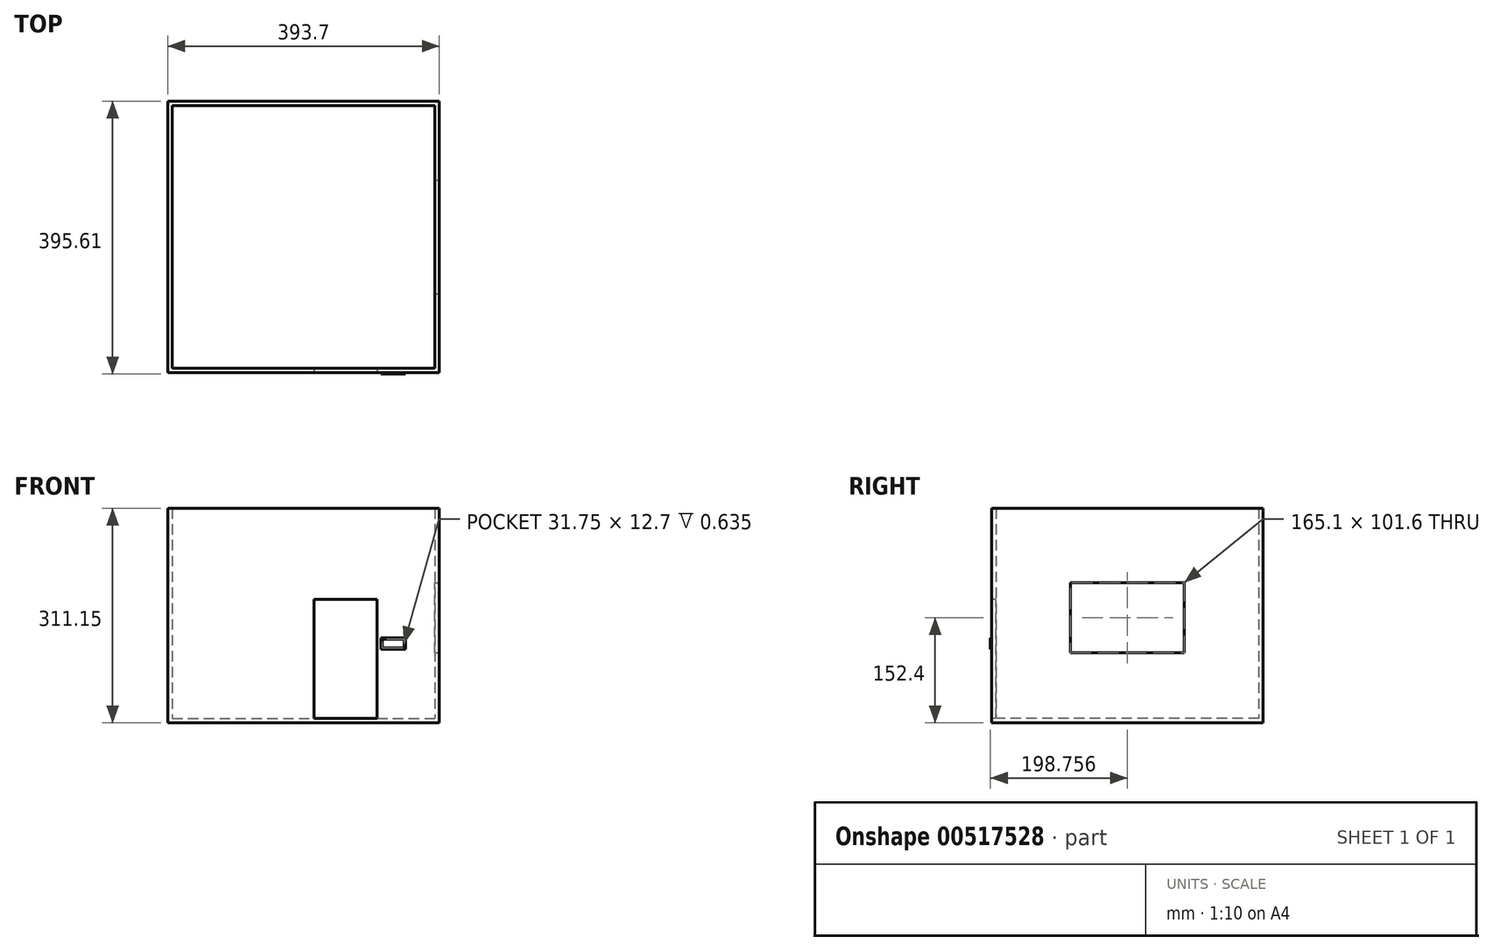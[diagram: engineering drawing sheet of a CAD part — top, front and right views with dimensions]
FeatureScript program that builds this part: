
annotation { "Feature Type Name" : "Feature", "Feature Type Description" : "" }
export const myFeature = defineFeature(function(context is Context, id is Id, definition is map)
    precondition{}
    {
        {
            var Q0;
            Q0=qCreatedBy(makeId("Top.planeOp"),FACE);
            var sketch = newSketch(context, id + "F0", { "sketchPlane" : qUnion([Q0])});
            skLineSegment(sketch, "E0.bottom", {"start": v(-199.94, 305.49) * mm, "end": v(181.06, 305.49) * mm});
            skLineSegment(sketch, "E0.top", {"start": v(-199.94, -75.51) * mm, "end": v(181.06, -75.51) * mm});
            skLineSegment(sketch, "E0.left", {"start": v(-199.94, 305.49) * mm, "end": v(-199.94, -75.51) * mm});
            skLineSegment(sketch, "E0.right", {"start": v(181.06, 305.49) * mm, "end": v(181.06, -75.51) * mm});
            skSolve(sketch);
        }
        {
            var Q0;
            Q0=makeQuery(id+"F0.imprint","IMPRINT",FACE,{"disambiguationData":[TD([[makeQuery(id+"F0.imprint","IMPRINT",EDGE,{"derivedFrom":sQuery(id+"F0.wireOp",EDGE,"E0.bottom")}),-1.0]])]});
            extrude(context, id + "F1", {"entities" : qUnion([Q0]), "depth" : 6.35 * mm, "offsetDistance" : 25.4 * mm});
        }
        {
            var Q0;
            Q0=makeQuery(id+"F1.opExtrude","CAP_FACE",FACE,{"disambiguationData":[OSD([sQuery(id+"F0.wireOp",EDGE,"E0.bottom"),sQuery(id+"F0.wireOp",EDGE,"E0.top"),sQuery(id+"F0.wireOp",EDGE,"E0.left"),sQuery(id+"F0.wireOp",EDGE,"E0.right")])],"isStart":false});
            var sketch = newSketch(context, id + "F2", { "sketchPlane" : qUnion([Q0])});
            skLineSegment(sketch, "E1.0", {"start": v(-206.29, 311.84) * mm, "end": v(187.41, 311.84) * mm});
            skLineSegment(sketch, "E1.1", {"start": v(-206.29, 311.84) * mm, "end": v(-206.29, -81.86) * mm});
            skLineSegment(sketch, "E1.2", {"start": v(-206.29, -81.86) * mm, "end": v(187.41, -81.86) * mm});
            skLineSegment(sketch, "E1.3", {"start": v(187.41, 311.84) * mm, "end": v(187.41, -81.86) * mm});
            skSolve(sketch);
        }
        {
            var Q0;
            Q0=makeQuery(id+"F2.imprint","IMPRINT",FACE,{"disambiguationData":[TD([[makeQuery(id+"F2.imprint","IMPRINT",EDGE,{"derivedFrom":sQuery(id+"F2.wireOp",EDGE,"E1.0")}),-1.0]])]});
            extrude(context, id + "F3", {"entities" : qUnion([Q0]), "operationType" : NewBodyOperationType.ADD, "depth" : 304.8 * mm, "offsetDistance" : 25.4 * mm, "hasSecondDirection" : true, "secondDirectionOppositeDirection" : true, "secondDirectionDepth" : 6.35 * mm});
        }
        {
            var Q0;
            Q0=makeQuery(id+"F3.opExtrude","SWEPT_FACE",FACE,{"disambiguationData":[OSD([sQuery(id+"F2.wireOp",EDGE,"E1.2")])]});
            var sketch = newSketch(context, id + "F4", { "sketchPlane" : qUnion([Q0])});
            skLineSegment(sketch, "E2.bottom", {"start": v(5.84, 179.07) * mm, "end": v(97.28, 179.07) * mm});
            skLineSegment(sketch, "E2.top", {"start": v(5.84, 6.35) * mm, "end": v(97.28, 6.35) * mm});
            skLineSegment(sketch, "E2.left", {"start": v(5.84, 179.07) * mm, "end": v(5.84, 6.35) * mm});
            skLineSegment(sketch, "E2.right", {"start": v(97.28, 179.07) * mm, "end": v(97.28, 6.35) * mm});
            skSolve(sketch);
        }
        {
            var Q0;
            Q0=makeQuery(id+"F4.imprint","IMPRINT",FACE,{"disambiguationData":[TD([[makeQuery(id+"F4.imprint","IMPRINT",EDGE,{"derivedFrom":sQuery(id+"F4.wireOp",EDGE,"E2.bottom")}),-1.0]])]});
            extrude(context, id + "F5", {"entities" : qUnion([Q0]), "operationType" : NewBodyOperationType.REMOVE, "oppositeDirection" : true, "depth" : 25.4 * mm, "offsetDistance" : 25.4 * mm});
        }
        {
            var Q0;
            Q0=makeQuery(id+"F3.opExtrude","SWEPT_FACE",FACE,{"disambiguationData":[OSD([sQuery(id+"F2.wireOp",EDGE,"E1.3")])]});
            var sketch = newSketch(context, id + "F6", { "sketchPlane" : qUnion([Q0])});
            skLineSegment(sketch, "E3", {"start": v(32.44, 101.6) * mm, "end": v(197.54, 101.6) * mm});
            skLineSegment(sketch, "E4", {"start": v(197.54, 101.6) * mm, "end": v(197.54, 152.4) * mm});
            skLineSegment(sketch, "E5", {"start": v(32.44, 101.6) * mm, "end": v(32.44, 155.58) * mm});
            skPoint(sketch, "E5.endSnap0", {"position": v(-81.86, 155.58) * mm});
            skLineSegment(sketch, "E6", {"start": v(197.54, 152.4) * mm, "end": v(32.44, 152.4) * mm});
            skLineSegment(sketch, "E7.MirrorCS", {"start": v(197.54, 203.2) * mm, "end": v(197.54, 152.4) * mm});
            skLineSegment(sketch, "E8.MirrorCS", {"start": v(32.44, 203.2) * mm, "end": v(197.54, 203.2) * mm});
            skLineSegment(sketch, "E9", {"start": v(32.44, 203.2) * mm, "end": v(32.44, 155.58) * mm});
            skSolve(sketch);
        }
        {
            var Q0;
            {var subQ0=sQuery(id+"F6.wireOp",EDGE,"E6");Q0=makeQuery(id+"F6.imprint","IMPRINT",FACE,{"disambiguationData":[TD([[makeQuery(id+"F6.imprint","IMPRINT",EDGE,{"derivedFrom":subQ0}),-1.0]])]});}
            var Q1;
            {var subQ0=sQuery(id+"F6.wireOp",EDGE,"E3");Q1=makeQuery(id+"F6.imprint","IMPRINT",FACE,{"disambiguationData":[TD([[makeQuery(id+"F6.imprint","IMPRINT",EDGE,{"derivedFrom":subQ0}),1.0]])]});}
            extrude(context, id + "F7", {"entities" : qUnion([Q0, Q1]), "operationType" : NewBodyOperationType.REMOVE, "oppositeDirection" : true, "depth" : 25.4 * mm, "offsetDistance" : 25.4 * mm});
        }
        {
            var Q0;
            Q0=makeQuery(id+"F3.opExtrude","SWEPT_FACE",FACE,{"disambiguationData":[OSD([sQuery(id+"F2.wireOp",EDGE,"E1.2")])]});
            var sketch = newSketch(context, id + "F8", { "sketchPlane" : qUnion([Q0])});
            skLineSegment(sketch, "E10.bottom", {"start": v(104.85, 120.98) * mm, "end": v(136.6, 120.98) * mm});
            skLineSegment(sketch, "E10.top", {"start": v(104.85, 108.28) * mm, "end": v(136.6, 108.28) * mm});
            skLineSegment(sketch, "E10.left", {"start": v(104.85, 120.98) * mm, "end": v(104.85, 108.28) * mm});
            skLineSegment(sketch, "E10.right", {"start": v(136.6, 120.98) * mm, "end": v(136.6, 108.28) * mm});
            skLineSegment(sketch, "E11.0", {"start": v(102.95, 122.88) * mm, "end": v(138.5, 122.88) * mm});
            skLineSegment(sketch, "E11.1", {"start": v(102.95, 122.88) * mm, "end": v(102.95, 106.37) * mm});
            skLineSegment(sketch, "E11.2", {"start": v(102.95, 106.37) * mm, "end": v(138.5, 106.37) * mm});
            skLineSegment(sketch, "E11.3", {"start": v(138.5, 122.88) * mm, "end": v(138.5, 106.37) * mm});
            skSolve(sketch);
        }
        {
            var Q0;
            Q0=makeQuery(id+"F8.imprint","IMPRINT",FACE,{"disambiguationData":[TD([[makeQuery(id+"F8.imprint","IMPRINT",EDGE,{"derivedFrom":sQuery(id+"F8.wireOp",EDGE,"E10.bottom")}),-1.0]])]});
            extrude(context, id + "F9", {"entities" : qUnion([Q0]), "operationType" : NewBodyOperationType.ADD, "depth" : 1.27 * mm, "offsetDistance" : 25.4 * mm});
        }
        {
            var Q0;
            Q0=makeQuery(id+"F8.imprint","IMPRINT",FACE,{"disambiguationData":[TD([[makeQuery(id+"F8.imprint","IMPRINT",EDGE,{"derivedFrom":sQuery(id+"F8.wireOp",EDGE,"E10.bottom")}),1.0]])]});
            extrude(context, id + "F10", {"entities" : qUnion([Q0]), "operationType" : NewBodyOperationType.ADD, "depth" : 1.9 * mm, "offsetDistance" : 25.4 * mm});
        }
    });
